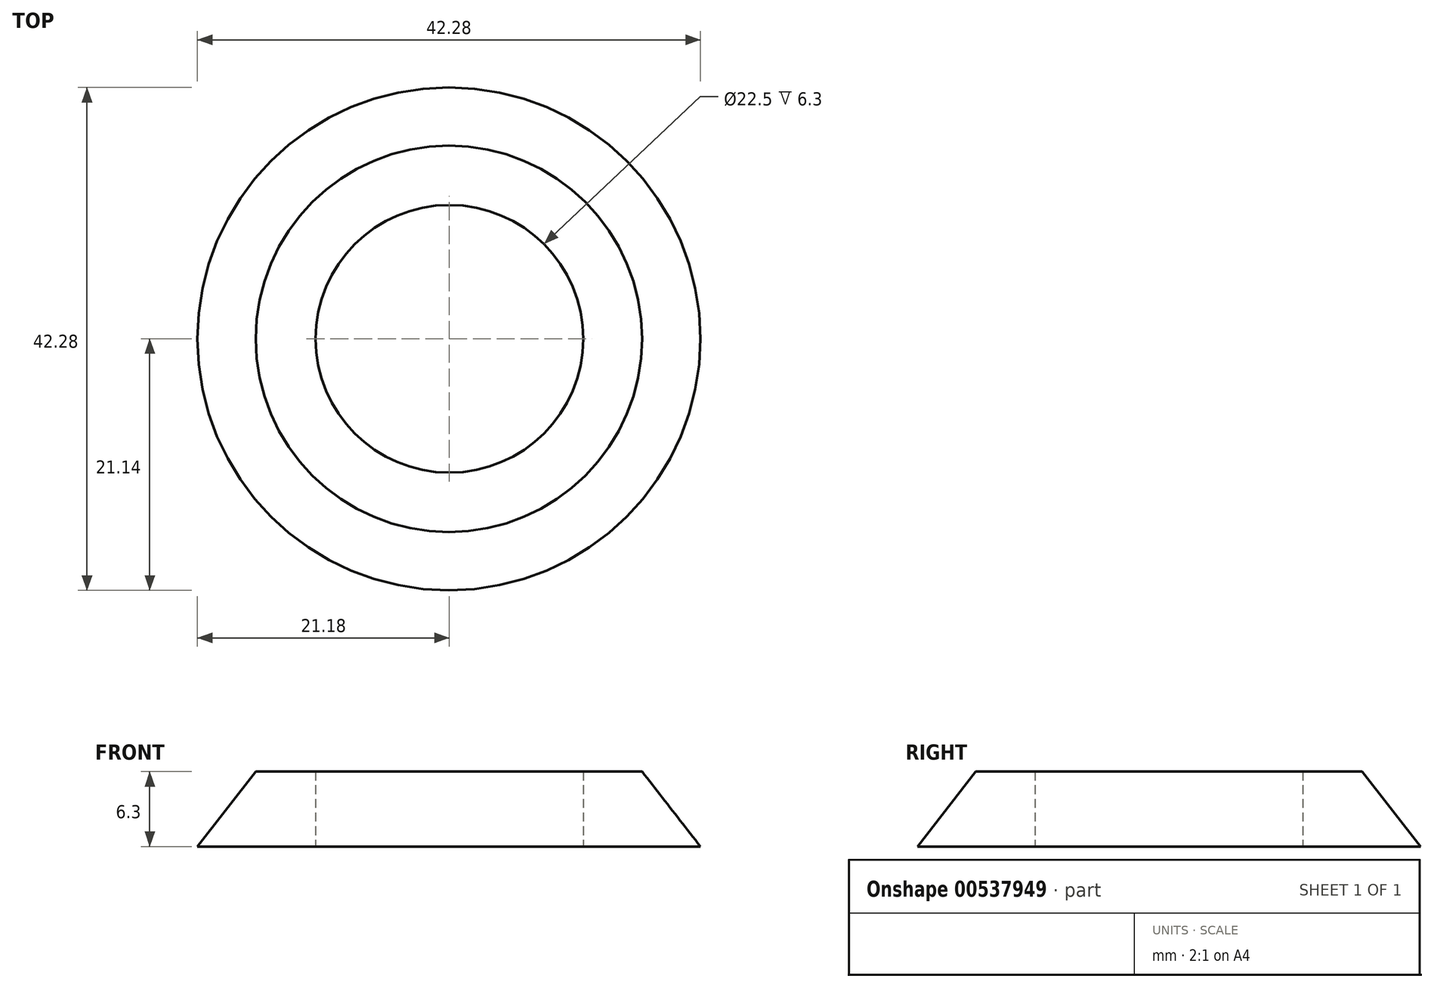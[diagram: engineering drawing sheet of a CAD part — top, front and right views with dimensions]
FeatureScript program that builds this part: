
annotation { "Feature Type Name" : "Feature", "Feature Type Description" : "" }
export const myFeature = defineFeature(function(context is Context, id is Id, definition is map)
    precondition{}
    {
        {
            var Q0;
            Q0=qCreatedBy(makeId("Front.planeOp"),FACE);
            var sketch = newSketch(context, id + "F0", { "sketchPlane" : qUnion([Q0])});
            skLineSegment(sketch, "E0", {"start": v(-0.04, 31.73) * mm, "end": v(-0.04, -23.13) * mm, "construction": true});
            skLineSegment(sketch, "E1", {"start": v(0, 0) * mm, "end": v(21.1, 0) * mm});
            skLineSegment(sketch, "E2.bottom", {"start": v(0, 0) * mm, "end": v(4.75, 0) * mm});
            skLineSegment(sketch, "E2.left", {"start": v(0, 0) * mm, "end": v(0, 6.3) * mm});
            skLineSegment(sketch, "E3", {"start": v(0, 6.3) * mm, "end": v(16.2, 6.3) * mm});
            skLineSegment(sketch, "E4", {"start": v(16.2, 6.3) * mm, "end": v(21.1, 0) * mm});
            skSolve(sketch);
        }
        {
            var Q0;
            Q0 = qSketchRegion(id + "F0", true);
            var Q1;
            Q1=sQuery(id+"F0.wireOp",EDGE,"E0");
            revolve(context, id + "F1", {"entities" : qUnion([Q0]), "axis" : qUnion([Q1]), "revolveType" : RevolveType.FULL});
        }
        {
            var Q0;
            Q0=makeQuery(id+"F1.opRevolve","SWEPT_FACE",FACE,{"disambiguationData":[OSD([sQuery(id+"F0.wireOp",EDGE,"E1"),sQuery(id+"F0.wireOp",EDGE,"E2.bottom")])]});
            var sketch = newSketch(context, id + "F2", { "sketchPlane" : qUnion([Q0])});
            skCircle(sketch, "E5", {"center": v(0, 0) * mm, "radius": 11.25 * mm});
            skSolve(sketch);
        }
        {
            var Q0;
            Q0=makeQuery(id+"F2.imprint","IMPRINT",FACE,{"disambiguationData":[TD([[makeQuery(id+"F2.imprint","IMPRINT",EDGE,{"derivedFrom":sQuery(id+"F2.wireOp",EDGE,"E5")}),1.0]])]});
            extrude(context, id + "F3", {"entities" : qUnion([Q0]), "operationType" : NewBodyOperationType.REMOVE, "oppositeDirection" : true, "depth" : 7 * mm, "offsetDistance" : 25 * mm});
        }
    });
